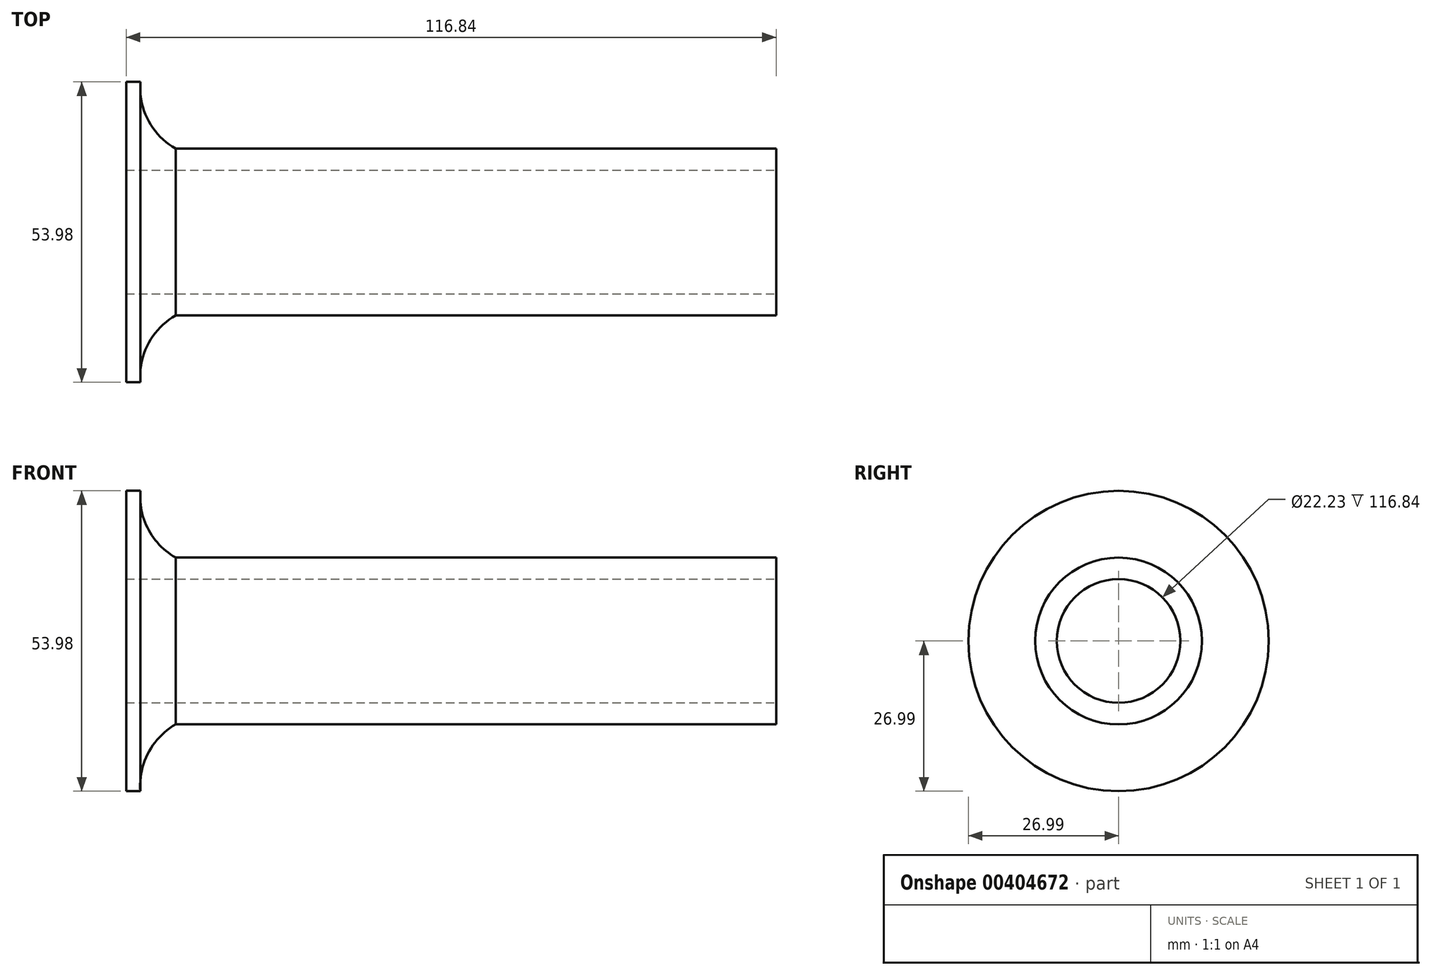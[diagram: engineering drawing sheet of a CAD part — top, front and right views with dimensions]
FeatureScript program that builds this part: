
annotation { "Feature Type Name" : "Feature", "Feature Type Description" : "" }
export const myFeature = defineFeature(function(context is Context, id is Id, definition is map)
    precondition{}
    {
        {
            var Q0;
            Q0=qCreatedBy(makeId("Front.planeOp"),FACE);
            var sketch = newSketch(context, id + "F0", { "sketchPlane" : qUnion([Q0])});
            skLineSegment(sketch, "E0", {"start": v(0, 14.99) * mm, "end": v(-107.95, 14.99) * mm});
            skArc(sketch, "E1", {"start": v(-114.3, 26.99) * mm, "mid": v(-112.86, 20.07) * mm, "end": v(-107.95, 14.99) * mm});
            skLineSegment(sketch, "E2", {"start": v(0, 0) * mm, "end": v(-194.6, 0) * mm, "construction": true});
            skLineSegment(sketch, "E3", {"start": v(-114.3, 26.99) * mm, "end": v(-116.84, 26.99) * mm});
            skLineSegment(sketch, "E4", {"start": v(-116.84, 26.99) * mm, "end": v(-116.84, 0) * mm});
            skLineSegment(sketch, "E5", {"start": v(0, 14.99) * mm, "end": v(0, 0) * mm});
            skLineSegment(sketch, "E6", {"start": v(-116.84, 0) * mm, "end": v(0, 0) * mm});
            skSolve(sketch);
        }
        {
            var Q0;
            Q0=makeQuery(id+"F0.imprint","IMPRINT",FACE,{"disambiguationData":[TD([[makeQuery(id+"F0.imprint","IMPRINT",EDGE,{"derivedFrom":sQuery(id+"F0.wireOp",EDGE,"E0")}),1.0]])]});
            var Q1;
            Q1=sQuery(id+"F0.wireOp",EDGE,"E2");
            revolve(context, id + "F1", {"entities" : qUnion([Q0]), "axis" : qUnion([Q1]), "revolveType" : RevolveType.FULL});
        }
        {
            var Q0;
            Q0=makeQuery(id+"F1.opRevolve","SWEPT_FACE",FACE,{"disambiguationData":[OSD([sQuery(id+"F0.wireOp",EDGE,"E5")])]});
            var sketch = newSketch(context, id + "F2", { "sketchPlane" : qUnion([Q0])});
            skCircle(sketch, "E7", {"center": v(0, 0) * mm, "radius": 11.11 * mm});
            skSolve(sketch);
        }
        {
            var Q0;
            Q0=makeQuery(id+"F2.imprint","IMPRINT",FACE,{"disambiguationData":[TD([[makeQuery(id+"F2.imprint","IMPRINT",EDGE,{"derivedFrom":sQuery(id+"F2.wireOp",EDGE,"E7")}),1.0]])]});
            extrude(context, id + "F3", {"entities" : qUnion([Q0]), "operationType" : NewBodyOperationType.REMOVE, "endBound" : BoundingType.THROUGH_ALL, "oppositeDirection" : true, "depth" : 25.4 * mm});
        }
    });
